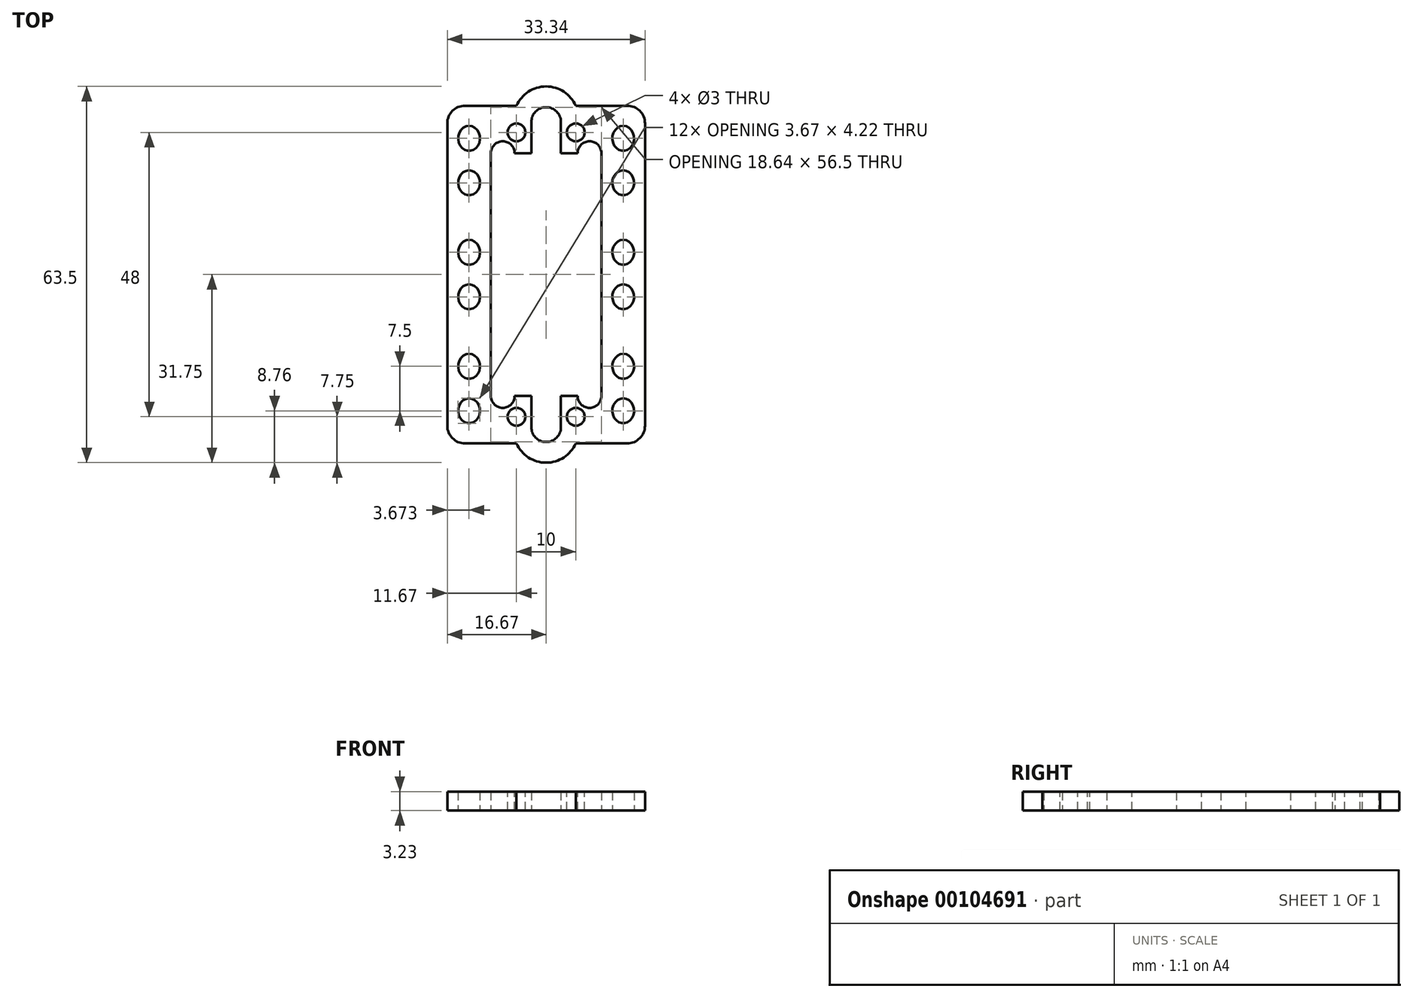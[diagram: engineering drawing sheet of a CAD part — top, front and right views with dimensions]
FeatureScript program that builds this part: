
annotation { "Feature Type Name" : "Feature", "Feature Type Description" : "" }
export const myFeature = defineFeature(function(context is Context, id is Id, definition is map)
    precondition{}
    {
        {
            var Q0;
            Q0=qCreatedBy(makeId("Top.planeOp"),FACE);
            var sketch = newSketch(context, id + "F0", { "sketchPlane" : qUnion([Q0])});
            skLineSegment(sketch, "E0.bottom", {"start": v(-16.67, 28.5) * mm, "end": v(-5, 28.5) * mm});
            skLineSegment(sketch, "E0.top", {"start": v(-16.68, -28.5) * mm, "end": v(-5, -28.5) * mm});
            skLineSegment(sketch, "E0.left", {"start": v(-16.67, 28.5) * mm, "end": v(-16.68, -28.5) * mm});
            skLineSegment(sketch, "E0.right", {"start": v(16.68, 28.5) * mm, "end": v(16.67, -28.5) * mm});
            skPoint(sketch, "E0.middle", {"position": v(0, 0) * mm});
            skLineSegment(sketch, "E1.bottom", {"start": v(-9.32, 20.5) * mm, "end": v(-2.5, 20.5) * mm});
            skLineSegment(sketch, "E1.top", {"start": v(-9.32, -20.5) * mm, "end": v(-2.5, -20.5) * mm});
            skLineSegment(sketch, "E1.left", {"start": v(-9.32, 20.5) * mm, "end": v(-9.32, -20.5) * mm});
            skLineSegment(sketch, "E1.right", {"start": v(9.32, 20.5) * mm, "end": v(9.32, -20.5) * mm});
            skLineSegment(sketch, "E2", {"start": v(-2.5, 20.5) * mm, "end": v(-2.5, 25.75) * mm});
            skLineSegment(sketch, "E3", {"start": v(2.5, 20.5) * mm, "end": v(2.5, 25.75) * mm});
            skArc(sketch, "E4", {"start": v(2.5, 25.75) * mm, "mid": v(0, 28.25) * mm, "end": v(-2.5, 25.75) * mm});
            skLineSegment(sketch, "E5.trimOffspring", {"start": v(2.5, 20.5) * mm, "end": v(9.32, 20.5) * mm});
            skLineSegment(sketch, "E6.trimOffspring", {"start": v(5, 28.5) * mm, "end": v(16.68, 28.5) * mm});
            skArc(sketch, "E7", {"start": v(5, 28.5) * mm, "mid": v(0, 31.75) * mm, "end": v(-5, 28.5) * mm});
            skLineSegment(sketch, "E8", {"start": v(-2.5, -20.5) * mm, "end": v(-2.5, -25.75) * mm});
            skLineSegment(sketch, "E9", {"start": v(2.5, -20.5) * mm, "end": v(2.5, -25.75) * mm});
            skArc(sketch, "E10", {"start": v(-2.5, -25.75) * mm, "mid": v(0, -28.25) * mm, "end": v(2.5, -25.75) * mm});
            skLineSegment(sketch, "E11.trimOffspring", {"start": v(5, -28.5) * mm, "end": v(16.67, -28.5) * mm});
            skLineSegment(sketch, "E12.trimOffspring", {"start": v(2.5, -20.5) * mm, "end": v(9.32, -20.5) * mm});
            skArc(sketch, "E13", {"start": v(-5, -28.5) * mm, "mid": v(0, -31.75) * mm, "end": v(5, -28.5) * mm});
            skPoint(sketch, "E14.endSnap0", {"position": v(10.84, -28.5) * mm});
            skSolve(sketch);
        }
        {
            var Q0;
            Q0 = qSketchRegion(id + "F0", true);
            extrude(context, id + "F1", {"entities" : qUnion([Q0]), "depth" : 3.23 * mm});
        }
        {
            var Q0;
            Q0=makeQuery(id+"F1.opExtrude","SWEPT_EDGE",EDGE,{"disambiguationData":[OSD([sQuery(id+"F0.wireOp",EDGE,"E0.right"),sQuery(id+"F0.wireOp",EDGE,"E6.trimOffspring")])]});
            var Q1;
            Q1=makeQuery(id+"F1.opExtrude","SWEPT_EDGE",EDGE,{"disambiguationData":[OSD([sQuery(id+"F0.wireOp",EDGE,"E0.bottom"),sQuery(id+"F0.wireOp",EDGE,"E0.left")])]});
            var Q2;
            Q2=makeQuery(id+"F1.opExtrude","SWEPT_EDGE",EDGE,{"disambiguationData":[OSD([sQuery(id+"F0.wireOp",EDGE,"E0.top"),sQuery(id+"F0.wireOp",EDGE,"E0.left")])]});
            var Q3;
            Q3=makeQuery(id+"F1.opExtrude","SWEPT_EDGE",EDGE,{"disambiguationData":[OSD([sQuery(id+"F0.wireOp",EDGE,"E0.right"),sQuery(id+"F0.wireOp",EDGE,"E11.trimOffspring")])]});
            fillet(context, id + "F2", {"entities" : qUnion([Q0, Q1, Q2, Q3]), "radius" : 3 * mm, "tangentPropagation" : true, "allowEdgeOverflow" : false});
        }
        {
            var Q0;
            Q0=makeQuery(id+"F1.opExtrude","CAP_FACE",FACE,{"disambiguationData":[OSD([sQuery(id+"F0.wireOp",EDGE,"E0.bottom"),sQuery(id+"F0.wireOp",EDGE,"E0.top"),sQuery(id+"F0.wireOp",EDGE,"E0.left"),sQuery(id+"F0.wireOp",EDGE,"E0.right"),sQuery(id+"F0.wireOp",EDGE,"E1.bottom"),sQuery(id+"F0.wireOp",EDGE,"E1.top"),sQuery(id+"F0.wireOp",EDGE,"E1.left"),sQuery(id+"F0.wireOp",EDGE,"E1.right"),sQuery(id+"F0.wireOp",EDGE,"E2"),sQuery(id+"F0.wireOp",EDGE,"E3"),sQuery(id+"F0.wireOp",EDGE,"E4"),sQuery(id+"F0.wireOp",EDGE,"E5.trimOffspring"),sQuery(id+"F0.wireOp",EDGE,"E6.trimOffspring"),sQuery(id+"F0.wireOp",EDGE,"E7"),sQuery(id+"F0.wireOp",EDGE,"E8"),sQuery(id+"F0.wireOp",EDGE,"E9"),sQuery(id+"F0.wireOp",EDGE,"E10"),sQuery(id+"F0.wireOp",EDGE,"E11.trimOffspring"),sQuery(id+"F0.wireOp",EDGE,"E12.trimOffspring"),sQuery(id+"F0.wireOp",EDGE,"E13"),sQuery(id+"F0.wireOp",EDGE,"iQAEclRB-GZwZ-qVFj-eQR7-KO5UlXMPUt0p"),sQuery(id+"F0.wireOp",EDGE,"bfe5c595-3e96-427d-8e89-a86ce424749b.0.1.0"),sQuery(id+"F0.wireOp",EDGE,"24af22e9-7879-4e4e-9d28-a3c88a050247.0.1.0"),sQuery(id+"F0.wireOp",EDGE,"24af22e9-7879-4e4e-9d28-a3c88a050247.0.1.1"),sQuery(id+"F0.wireOp",EDGE,"24af22e9-7879-4e4e-9d28-a3c88a050247.0.2.0"),sQuery(id+"F0.wireOp",EDGE,"24af22e9-7879-4e4e-9d28-a3c88a050247.0.2.1"),sQuery(id+"F0.wireOp",EDGE,"24af22e9-7879-4e4e-9d28-a3c88a050247.1.0.0"),sQuery(id+"F0.wireOp",EDGE,"24af22e9-7879-4e4e-9d28-a3c88a050247.1.0.1"),sQuery(id+"F0.wireOp",EDGE,"24af22e9-7879-4e4e-9d28-a3c88a050247.1.1.0"),sQuery(id+"F0.wireOp",EDGE,"24af22e9-7879-4e4e-9d28-a3c88a050247.1.1.1"),sQuery(id+"F0.wireOp",EDGE,"24af22e9-7879-4e4e-9d28-a3c88a050247.1.2.0"),sQuery(id+"F0.wireOp",EDGE,"24af22e9-7879-4e4e-9d28-a3c88a050247.1.2.1")])],"isStart":false});
            var sketch = newSketch(context, id + "F3", { "sketchPlane" : qUnion([Q0])});
            skArc(sketch, "E15", {"start": v(-5.32, 20.5) * mm, "mid": v(-7.32, 22.5) * mm, "end": v(-9.32, 20.5) * mm});
            skArc(sketch, "E16", {"start": v(9.32, 20.5) * mm, "mid": v(7.32, 22.5) * mm, "end": v(5.32, 20.5) * mm});
            skArc(sketch, "E17", {"start": v(-9.32, -20.5) * mm, "mid": v(-7.32, -22.5) * mm, "end": v(-5.32, -20.5) * mm});
            skArc(sketch, "E18", {"start": v(5.32, -20.5) * mm, "mid": v(7.32, -22.5) * mm, "end": v(9.32, -20.5) * mm});
            skLineSegment(sketch, "E19", {"start": v(-9.32, 20.5) * mm, "end": v(-5.32, 20.5) * mm});
            skLineSegment(sketch, "E20", {"start": v(5.32, 20.5) * mm, "end": v(9.32, 20.5) * mm});
            skLineSegment(sketch, "E21", {"start": v(-9.32, -20.5) * mm, "end": v(-5.32, -20.5) * mm});
            skLineSegment(sketch, "E22", {"start": v(5.32, -20.5) * mm, "end": v(9.32, -20.5) * mm});
            skSolve(sketch);
        }
        {
            var Q0;
            Q0 = qSketchRegion(id + "F3", true);
            extrude(context, id + "F4", {"entities" : qUnion([Q0]), "operationType" : NewBodyOperationType.REMOVE, "endBound" : BoundingType.THROUGH_ALL, "oppositeDirection" : true, "depth" : 25 * mm});
        }
        {
            var Q0;
            Q0=makeQuery(id+"F1.opExtrude","CAP_FACE",FACE,{"disambiguationData":[OSD([sQuery(id+"F0.wireOp",EDGE,"E0.bottom"),sQuery(id+"F0.wireOp",EDGE,"E0.top"),sQuery(id+"F0.wireOp",EDGE,"E0.left"),sQuery(id+"F0.wireOp",EDGE,"E0.right"),sQuery(id+"F0.wireOp",EDGE,"E1.bottom"),sQuery(id+"F0.wireOp",EDGE,"E1.top"),sQuery(id+"F0.wireOp",EDGE,"E1.left"),sQuery(id+"F0.wireOp",EDGE,"E1.right"),sQuery(id+"F0.wireOp",EDGE,"E2"),sQuery(id+"F0.wireOp",EDGE,"E3"),sQuery(id+"F0.wireOp",EDGE,"E4"),sQuery(id+"F0.wireOp",EDGE,"E5.trimOffspring"),sQuery(id+"F0.wireOp",EDGE,"E6.trimOffspring"),sQuery(id+"F0.wireOp",EDGE,"E7"),sQuery(id+"F0.wireOp",EDGE,"E8"),sQuery(id+"F0.wireOp",EDGE,"E9"),sQuery(id+"F0.wireOp",EDGE,"E10"),sQuery(id+"F0.wireOp",EDGE,"E11.trimOffspring"),sQuery(id+"F0.wireOp",EDGE,"E12.trimOffspring"),sQuery(id+"F0.wireOp",EDGE,"E13"),sQuery(id+"F0.wireOp",EDGE,"iQAEclRB-GZwZ-qVFj-eQR7-KO5UlXMPUt0p"),sQuery(id+"F0.wireOp",EDGE,"bfe5c595-3e96-427d-8e89-a86ce424749b.0.1.0"),sQuery(id+"F0.wireOp",EDGE,"24af22e9-7879-4e4e-9d28-a3c88a050247.0.1.0"),sQuery(id+"F0.wireOp",EDGE,"24af22e9-7879-4e4e-9d28-a3c88a050247.0.1.1"),sQuery(id+"F0.wireOp",EDGE,"24af22e9-7879-4e4e-9d28-a3c88a050247.0.2.0"),sQuery(id+"F0.wireOp",EDGE,"24af22e9-7879-4e4e-9d28-a3c88a050247.0.2.1"),sQuery(id+"F0.wireOp",EDGE,"24af22e9-7879-4e4e-9d28-a3c88a050247.1.0.0"),sQuery(id+"F0.wireOp",EDGE,"24af22e9-7879-4e4e-9d28-a3c88a050247.1.0.1"),sQuery(id+"F0.wireOp",EDGE,"24af22e9-7879-4e4e-9d28-a3c88a050247.1.1.0"),sQuery(id+"F0.wireOp",EDGE,"24af22e9-7879-4e4e-9d28-a3c88a050247.1.1.1"),sQuery(id+"F0.wireOp",EDGE,"24af22e9-7879-4e4e-9d28-a3c88a050247.1.2.0"),sQuery(id+"F0.wireOp",EDGE,"24af22e9-7879-4e4e-9d28-a3c88a050247.1.2.1")])],"isStart":false});
            var sketch = newSketch(context, id + "F5", { "sketchPlane" : qUnion([Q0])});
            skCircle(sketch, "E23", {"center": v(-5, 24) * mm, "radius": 1.5 * mm});
            skCircle(sketch, "E24", {"center": v(5, 24) * mm, "radius": 1.5 * mm});
            skCircle(sketch, "E25", {"center": v(-5, -24) * mm, "radius": 1.5 * mm});
            skCircle(sketch, "E26", {"center": v(5, -24) * mm, "radius": 1.5 * mm});
            skSolve(sketch);
        }
        {
            var Q0;
            Q0 = qSketchRegion(id + "F5", true);
            extrude(context, id + "F6", {"entities" : qUnion([Q0]), "operationType" : NewBodyOperationType.REMOVE, "endBound" : BoundingType.THROUGH_ALL, "oppositeDirection" : true, "depth" : 25 * mm});
        }
        {
            var Q0;
            Q0=makeQuery(id+"F1.opExtrude","CAP_FACE",FACE,{"disambiguationData":[OSD([sQuery(id+"F0.wireOp",EDGE,"E0.bottom"),sQuery(id+"F0.wireOp",EDGE,"E0.top"),sQuery(id+"F0.wireOp",EDGE,"E0.left"),sQuery(id+"F0.wireOp",EDGE,"E0.right"),sQuery(id+"F0.wireOp",EDGE,"E1.bottom"),sQuery(id+"F0.wireOp",EDGE,"E1.top"),sQuery(id+"F0.wireOp",EDGE,"E1.left"),sQuery(id+"F0.wireOp",EDGE,"E1.right"),sQuery(id+"F0.wireOp",EDGE,"E2"),sQuery(id+"F0.wireOp",EDGE,"E3"),sQuery(id+"F0.wireOp",EDGE,"E4"),sQuery(id+"F0.wireOp",EDGE,"E5.trimOffspring"),sQuery(id+"F0.wireOp",EDGE,"E6.trimOffspring"),sQuery(id+"F0.wireOp",EDGE,"E7"),sQuery(id+"F0.wireOp",EDGE,"E8"),sQuery(id+"F0.wireOp",EDGE,"E9"),sQuery(id+"F0.wireOp",EDGE,"E10"),sQuery(id+"F0.wireOp",EDGE,"E11.trimOffspring"),sQuery(id+"F0.wireOp",EDGE,"E12.trimOffspring"),sQuery(id+"F0.wireOp",EDGE,"E13")])],"isStart":false});
            var sketch = newSketch(context, id + "F7", { "sketchPlane" : qUnion([Q0])});
            skLineSegment(sketch, "E27", {"start": v(0, 31.75) * mm, "end": v(0, -31.75) * mm, "construction": true});
            skLineSegment(sketch, "E28", {"start": v(-16.68, 0) * mm, "end": v(-9.32, 0) * mm, "construction": true});
            skLineSegment(sketch, "E29", {"start": v(-13, 28.5) * mm, "end": v(-13, -28.5) * mm, "construction": true});
            skPoint(sketch, "E29.endSnap0", {"position": v(-9.34, -28.5) * mm});
            skPoint(sketch, "E30", {"position": v(-13, 0) * mm});
            skEllipse(sketch, "E31.MirrorC", {"center": v(-13, 23) * mm, "majorRadius": 2.1 * mm, "minorRadius": 1.83 * mm, "majorAxis": v(0, 1)});
            skEllipse(sketch, "E32.MirrorC", {"center": v(-13, 15.5) * mm, "majorRadius": 2.1 * mm, "minorRadius": 1.83 * mm, "majorAxis": v(0, 1)});
            skEllipse(sketch, "E33.MirrorC", {"center": v(-13, 3.75) * mm, "majorRadius": 2.1 * mm, "minorRadius": 1.83 * mm, "majorAxis": v(0, 1)});
            skEllipse(sketch, "E34.MirrorC", {"center": v(-13, -3.75) * mm, "majorRadius": 2.1 * mm, "minorRadius": 1.83 * mm, "majorAxis": v(0, 1)});
            skEllipse(sketch, "E35.MirrorC", {"center": v(-13, -15.49) * mm, "majorRadius": 2.1 * mm, "minorRadius": 1.83 * mm, "majorAxis": v(0, 1)});
            skEllipse(sketch, "E36.MirrorC", {"center": v(-13, -22.99) * mm, "majorRadius": 2.1 * mm, "minorRadius": 1.83 * mm, "majorAxis": v(0, 1)});
            skEllipse(sketch, "E37.MirrorC", {"center": v(13, 23) * mm, "majorRadius": 2.1 * mm, "minorRadius": 1.83 * mm, "majorAxis": v(0, 1)});
            skEllipse(sketch, "E38.MirrorC", {"center": v(13, 15.5) * mm, "majorRadius": 2.1 * mm, "minorRadius": 1.83 * mm, "majorAxis": v(0, 1)});
            skEllipse(sketch, "E39.MirrorC", {"center": v(13, 3.75) * mm, "majorRadius": 2.1 * mm, "minorRadius": 1.83 * mm, "majorAxis": v(0, 1)});
            skEllipse(sketch, "E40.MirrorC", {"center": v(13, -3.75) * mm, "majorRadius": 2.1 * mm, "minorRadius": 1.83 * mm, "majorAxis": v(0, 1)});
            skEllipse(sketch, "E41.MirrorC", {"center": v(13, -15.49) * mm, "majorRadius": 2.1 * mm, "minorRadius": 1.83 * mm, "majorAxis": v(0, 1)});
            skEllipse(sketch, "E42.MirrorC", {"center": v(13, -22.99) * mm, "majorRadius": 2.1 * mm, "minorRadius": 1.83 * mm, "majorAxis": v(0, 1)});
            skSolve(sketch);
        }
        {
            var Q0;
            Q0 = qSketchRegion(id + "F7", true);
            extrude(context, id + "F8", {"entities" : qUnion([Q0]), "operationType" : NewBodyOperationType.REMOVE, "oppositeDirection" : true, "depth" : 25 * mm});
        }
    });
